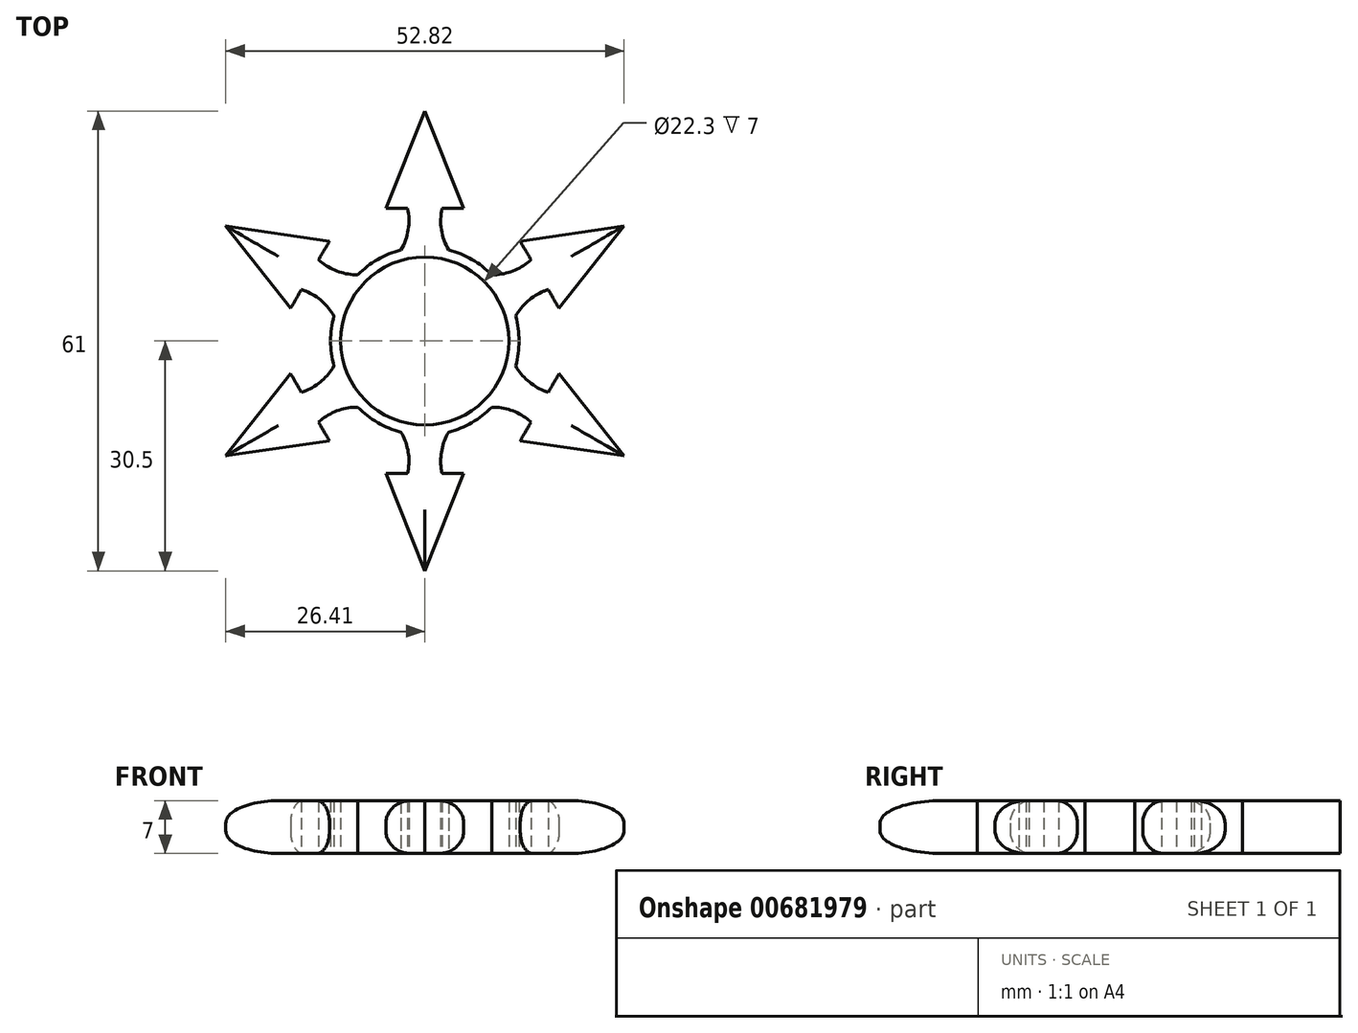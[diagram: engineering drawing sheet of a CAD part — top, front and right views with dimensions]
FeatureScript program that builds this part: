
annotation { "Feature Type Name" : "Feature", "Feature Type Description" : "" }
export const myFeature = defineFeature(function(context is Context, id is Id, definition is map)
    precondition{}
    {
        {
            var Q0;
            Q0=qCreatedBy(makeId("Top.planeOp"),FACE);
            var sketch = newSketch(context, id + "F0", { "sketchPlane" : qUnion([Q0])});
            skCircle(sketch, "E0", {"center": v(0, 0) * mm, "radius": 11.15 * mm});
            skArc(sketch, "E1", {"start": v(-5.16, 9.88) * mm, "mid": v(-2.58, 13.3) * mm, "end": v(-2.28, 17.58) * mm});
            skLineSegment(sketch, "E2", {"start": v(-2.28, 17.58) * mm, "end": v(-5.15, 17.58) * mm});
            skLineSegment(sketch, "E3", {"start": v(-5.15, 17.58) * mm, "end": v(0, 30.5) * mm});
            skLineSegment(sketch, "E4.MirrorCS", {"start": v(2.28, 17.58) * mm, "end": v(5.15, 17.58) * mm});
            skArc(sketch, "E5.MirrorCS", {"start": v(5.16, 9.88) * mm, "mid": v(2.58, 13.3) * mm, "end": v(2.28, 17.58) * mm});
            skLineSegment(sketch, "E6.MirrorCS", {"start": v(5.15, 17.58) * mm, "end": v(0, 30.5) * mm});
            skLineSegment(sketch, "E7.MirrorCS", {"start": v(-2.28, -17.58) * mm, "end": v(-5.15, -17.58) * mm});
            skLineSegment(sketch, "E8.MirrorCS", {"start": v(2.28, -17.58) * mm, "end": v(5.15, -17.58) * mm});
            skArc(sketch, "E9.MirrorCS", {"start": v(5.16, -9.88) * mm, "mid": v(2.58, -13.3) * mm, "end": v(2.28, -17.58) * mm});
            skArc(sketch, "E10.MirrorCS", {"start": v(-5.16, -9.88) * mm, "mid": v(-2.58, -13.3) * mm, "end": v(-2.28, -17.58) * mm});
            skLineSegment(sketch, "E11.MirrorCS", {"start": v(-5.15, -17.58) * mm, "end": v(0, -30.5) * mm});
            skLineSegment(sketch, "E12.MirrorCS", {"start": v(5.15, -17.58) * mm, "end": v(0, -30.5) * mm});
            skLineSegment(sketch, "E13.1.0", {"start": v(17.8, -4.33) * mm, "end": v(26.41, -15.25) * mm});
            skLineSegment(sketch, "E13.1.1", {"start": v(12.65, -13.26) * mm, "end": v(26.41, -15.25) * mm});
            skLineSegment(sketch, "E13.1.2", {"start": v(14.09, -10.77) * mm, "end": v(12.65, -13.26) * mm});
            skArc(sketch, "E13.1.3", {"start": v(5.98, -9.41) * mm, "mid": v(10.23, -8.89) * mm, "end": v(14.09, -10.77) * mm});
            skArc(sketch, "E13.1.4", {"start": v(11.14, -0.47) * mm, "mid": v(12.82, -4.42) * mm, "end": v(16.37, -6.81) * mm});
            skLineSegment(sketch, "E13.1.5", {"start": v(16.37, -6.81) * mm, "end": v(17.8, -4.33) * mm});
            skLineSegment(sketch, "E13.2.0", {"start": v(12.65, 13.26) * mm, "end": v(26.41, 15.25) * mm});
            skLineSegment(sketch, "E13.2.1", {"start": v(17.8, 4.33) * mm, "end": v(26.41, 15.25) * mm});
            skLineSegment(sketch, "E13.2.2", {"start": v(16.37, 6.81) * mm, "end": v(17.8, 4.33) * mm});
            skArc(sketch, "E13.2.3", {"start": v(11.14, 0.47) * mm, "mid": v(12.82, 4.42) * mm, "end": v(16.37, 6.81) * mm});
            skArc(sketch, "E13.2.4", {"start": v(5.98, 9.41) * mm, "mid": v(10.23, 8.89) * mm, "end": v(14.09, 10.77) * mm});
            skLineSegment(sketch, "E13.2.5", {"start": v(14.09, 10.77) * mm, "end": v(12.65, 13.26) * mm});
            skLineSegment(sketch, "E13.4.0", {"start": v(-17.8, 4.33) * mm, "end": v(-26.41, 15.25) * mm});
            skLineSegment(sketch, "E13.4.1", {"start": v(-12.65, 13.26) * mm, "end": v(-26.41, 15.25) * mm});
            skLineSegment(sketch, "E13.4.2", {"start": v(-14.09, 10.77) * mm, "end": v(-12.65, 13.26) * mm});
            skArc(sketch, "E13.4.3", {"start": v(-5.98, 9.41) * mm, "mid": v(-10.23, 8.89) * mm, "end": v(-14.09, 10.77) * mm});
            skArc(sketch, "E13.4.4", {"start": v(-11.14, 0.47) * mm, "mid": v(-12.82, 4.42) * mm, "end": v(-16.37, 6.81) * mm});
            skLineSegment(sketch, "E13.4.5", {"start": v(-16.37, 6.81) * mm, "end": v(-17.8, 4.33) * mm});
            skLineSegment(sketch, "E13.5.0", {"start": v(-12.65, -13.26) * mm, "end": v(-26.41, -15.25) * mm});
            skLineSegment(sketch, "E13.5.1", {"start": v(-17.8, -4.33) * mm, "end": v(-26.41, -15.25) * mm});
            skLineSegment(sketch, "E13.5.2", {"start": v(-16.37, -6.81) * mm, "end": v(-17.8, -4.33) * mm});
            skArc(sketch, "E13.5.3", {"start": v(-11.14, -0.47) * mm, "mid": v(-12.82, -4.42) * mm, "end": v(-16.37, -6.81) * mm});
            skArc(sketch, "E13.5.4", {"start": v(-5.98, -9.41) * mm, "mid": v(-10.23, -8.89) * mm, "end": v(-14.09, -10.77) * mm});
            skLineSegment(sketch, "E13.5.5", {"start": v(-14.09, -10.77) * mm, "end": v(-12.65, -13.26) * mm});
            skCircle(sketch, "E14", {"center": v(0, 0) * mm, "radius": 12.5 * mm});
            skSolve(sketch);
        }
        {
            var Q0;
            Q0 = qSketchRegion(id + "F0", true);
            extrude(context, id + "F1", {"entities" : qUnion([Q0]), "depth" : 7 * mm, "offsetDistance" : 25 * mm});
        }
        {
            var Q0;
            Q0=makeQuery(id+"F1.opExtrude","CAP_EDGE",EDGE,{"disambiguationData":[OSD([sQuery(id+"F0.wireOp",EDGE,"E13.5.0")])],"isStart":true});
            var Q1;
            Q1=makeQuery(id+"F1.opExtrude","CAP_EDGE",EDGE,{"disambiguationData":[OSD([sQuery(id+"F0.wireOp",EDGE,"E13.5.1")])],"isStart":true});
            var Q2;
            Q2=makeQuery(id+"F1.opExtrude","CAP_EDGE",EDGE,{"disambiguationData":[OSD([sQuery(id+"F0.wireOp",EDGE,"E13.4.0")])],"isStart":true});
            var Q3;
            Q3=makeQuery(id+"F1.opExtrude","CAP_EDGE",EDGE,{"disambiguationData":[OSD([sQuery(id+"F0.wireOp",EDGE,"E13.4.1")])],"isStart":true});
            var Q4;
            Q4=makeQuery(id+"F1.opExtrude","CAP_EDGE",EDGE,{"disambiguationData":[OSD([sQuery(id+"F0.wireOp",EDGE,"E3")])],"isStart":true});
            var Q5;
            Q5=makeQuery(id+"F1.opExtrude","CAP_EDGE",EDGE,{"disambiguationData":[OSD([sQuery(id+"F0.wireOp",EDGE,"E13.2.0")])],"isStart":true});
            var Q6;
            Q6=makeQuery(id+"F1.opExtrude","CAP_EDGE",EDGE,{"disambiguationData":[OSD([sQuery(id+"F0.wireOp",EDGE,"E13.2.1")])],"isStart":true});
            var Q7;
            Q7=makeQuery(id+"F1.opExtrude","CAP_EDGE",EDGE,{"disambiguationData":[OSD([sQuery(id+"F0.wireOp",EDGE,"E13.1.0")])],"isStart":true});
            var Q8;
            Q8=makeQuery(id+"F1.opExtrude","CAP_EDGE",EDGE,{"disambiguationData":[OSD([sQuery(id+"F0.wireOp",EDGE,"E13.1.1")])],"isStart":true});
            var Q9;
            Q9=makeQuery(id+"F1.opExtrude","CAP_EDGE",EDGE,{"disambiguationData":[OSD([sQuery(id+"F0.wireOp",EDGE,"E11.MirrorCS")])],"isStart":true});
            var Q10;
            Q10=makeQuery(id+"F1.opExtrude","CAP_EDGE",EDGE,{"disambiguationData":[OSD([sQuery(id+"F0.wireOp",EDGE,"E12.MirrorCS")])],"isStart":true});
            var Q11;
            Q11=makeQuery(id+"F1.opExtrude","CAP_EDGE",EDGE,{"disambiguationData":[OSD([sQuery(id+"F0.wireOp",EDGE,"E6.MirrorCS")])],"isStart":true});
            var Q12;
            Q12=makeQuery(id+"F1.opExtrude","CAP_EDGE",EDGE,{"disambiguationData":[OSD([sQuery(id+"F0.wireOp",EDGE,"E13.4.1")])],"isStart":false});
            var Q13;
            Q13=makeQuery(id+"F1.opExtrude","CAP_EDGE",EDGE,{"disambiguationData":[OSD([sQuery(id+"F0.wireOp",EDGE,"E13.4.0")])],"isStart":false});
            var Q14;
            Q14=makeQuery(id+"F1.opExtrude","CAP_EDGE",EDGE,{"disambiguationData":[OSD([sQuery(id+"F0.wireOp",EDGE,"E3")])],"isStart":false});
            var Q15;
            Q15=makeQuery(id+"F1.opExtrude","CAP_EDGE",EDGE,{"disambiguationData":[OSD([sQuery(id+"F0.wireOp",EDGE,"E6.MirrorCS")])],"isStart":false});
            var Q16;
            Q16=makeQuery(id+"F1.opExtrude","CAP_EDGE",EDGE,{"disambiguationData":[OSD([sQuery(id+"F0.wireOp",EDGE,"E13.2.1")])],"isStart":false});
            var Q17;
            Q17=makeQuery(id+"F1.opExtrude","CAP_EDGE",EDGE,{"disambiguationData":[OSD([sQuery(id+"F0.wireOp",EDGE,"E13.1.0")])],"isStart":false});
            var Q18;
            Q18=makeQuery(id+"F1.opExtrude","CAP_EDGE",EDGE,{"disambiguationData":[OSD([sQuery(id+"F0.wireOp",EDGE,"E13.1.1")])],"isStart":false});
            var Q19;
            Q19=makeQuery(id+"F1.opExtrude","CAP_EDGE",EDGE,{"disambiguationData":[OSD([sQuery(id+"F0.wireOp",EDGE,"E12.MirrorCS")])],"isStart":false});
            var Q20;
            Q20=makeQuery(id+"F1.opExtrude","CAP_EDGE",EDGE,{"disambiguationData":[OSD([sQuery(id+"F0.wireOp",EDGE,"E11.MirrorCS")])],"isStart":false});
            var Q21;
            Q21=makeQuery(id+"F1.opExtrude","CAP_EDGE",EDGE,{"disambiguationData":[OSD([sQuery(id+"F0.wireOp",EDGE,"E13.5.1")])],"isStart":false});
            var Q22;
            Q22=makeQuery(id+"F1.opExtrude","CAP_EDGE",EDGE,{"disambiguationData":[OSD([sQuery(id+"F0.wireOp",EDGE,"E13.5.0")])],"isStart":false});
            var Q23;
            Q23=makeQuery(id+"F1.opExtrude","CAP_EDGE",EDGE,{"disambiguationData":[OSD([sQuery(id+"F0.wireOp",EDGE,"E13.2.0")])],"isStart":false});
            fillet(context, id + "F2", {"entities" : qUnion([Q0, Q1, Q2, Q3, Q4, Q5, Q6, Q7, Q8, Q9, Q10, Q11, Q12, Q13, Q14, Q15, Q16, Q17, Q18, Q19, Q20, Q21, Q22, Q23]), "radius" : 3 * mm, "tangentPropagation" : true, "allowEdgeOverflow" : false});
        }
    });
